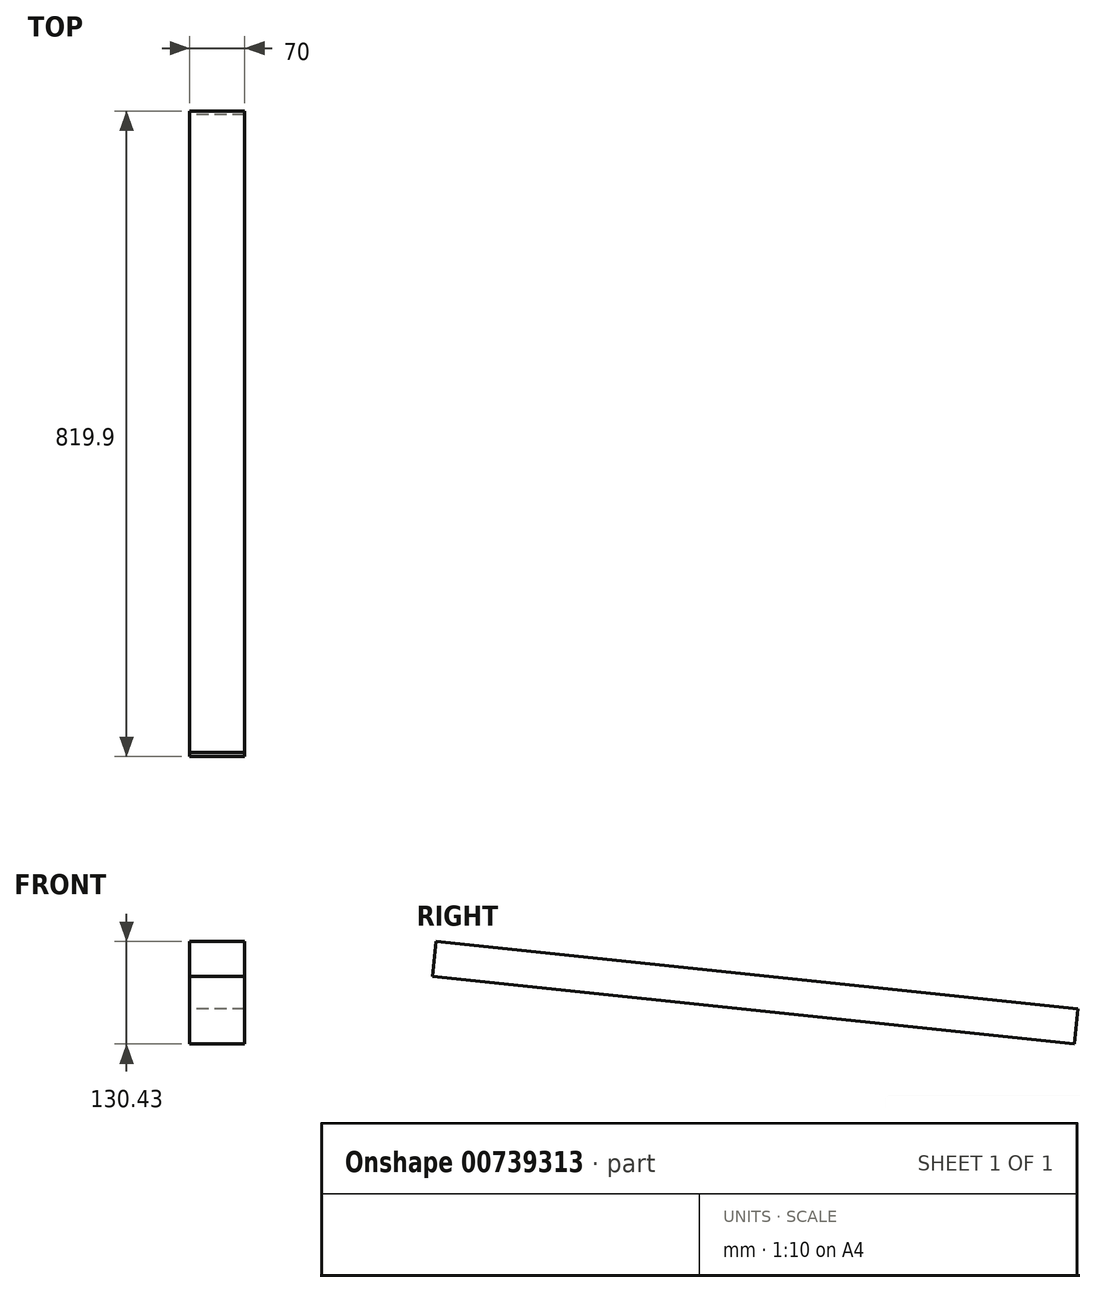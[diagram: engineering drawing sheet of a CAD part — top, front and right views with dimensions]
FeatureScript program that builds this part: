
annotation { "Feature Type Name" : "Feature", "Feature Type Description" : "" }
export const myFeature = defineFeature(function(context is Context, id is Id, definition is map)
    precondition{}
    {
        {
            var Q0;
            Q0=qCreatedBy(makeId("Right.planeOp"),FACE);
            var sketch = newSketch(context, id + "F0", { "sketchPlane" : qUnion([Q0])});
            skLineSegment(sketch, "E0", {"start": v(0, 0) * mm, "end": v(4.7, 44.75) * mm});
            skLineSegment(sketch, "E1", {"start": v(4.7, 44.75) * mm, "end": v(819.9, -40.93) * mm});
            skLineSegment(sketch, "E2", {"start": v(819.9, -40.93) * mm, "end": v(815.2, -85.68) * mm});
            skLineSegment(sketch, "E3", {"start": v(815.2, -85.68) * mm, "end": v(0, 0) * mm});
            skLineSegment(sketch, "E4", {"start": v(819.9, -40.93) * mm, "end": v(859.95, -45.14) * mm, "construction": true});
            skLineSegment(sketch, "E5", {"start": v(859.95, -45.14) * mm, "end": v(859.95, -90.38) * mm, "construction": true});
            skLineSegment(sketch, "E6", {"start": v(859.95, -90.38) * mm, "end": v(815.2, -85.68) * mm, "construction": true});
            skLineSegment(sketch, "E7", {"start": v(4.7, 44.75) * mm, "end": v(-40.05, 49.46) * mm, "construction": true});
            skLineSegment(sketch, "E8", {"start": v(-40.05, 49.46) * mm, "end": v(-40.05, 4.2) * mm, "construction": true});
            skLineSegment(sketch, "E9", {"start": v(-40.05, 4.2) * mm, "end": v(0, 0) * mm, "construction": true});
            skSolve(sketch);
        }
        {
            var Q0;
            Q0=makeQuery(id+"F0.imprint","IMPRINT",FACE,{"disambiguationData":[TD([[makeQuery(id+"F0.imprint","IMPRINT",EDGE,{"derivedFrom":sQuery(id+"F0.wireOp",EDGE,"E0")}),-1.0]])]});
            extrude(context, id + "F1", {"entities" : qUnion([Q0]), "depth" : 70 * mm, "offsetDistance" : 25 * mm});
        }
    });
